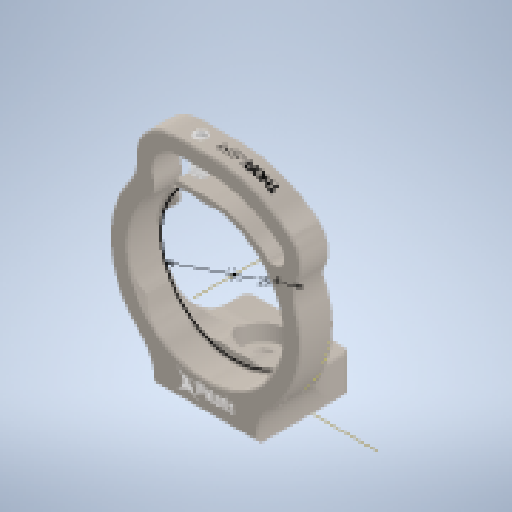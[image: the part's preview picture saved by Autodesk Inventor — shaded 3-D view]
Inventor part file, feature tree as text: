
AUTODESK INVENTOR PART (.ipt)
format: ipt  version: 2023 (Build 270158000, 158)  size: 2,079,232 bytes
history: native  units: mm
features: other x10, sketch x2
ambient origin geometry x8: Origin, YZ Plane, XZ Plane, XY Plane, X Axis, Y Axis, Z Axis, Center Point
bodies: Solid1 (feature_tree), Solid2 (feature_tree)
feature tree (12):
  sketch  "Sketch1"  dims[d3=25.4mm]
  other  "Work Point1"
  other  "Work Point2"
  other  "Work Point4"
  other  "Work Axis1"
  other  "Work Point7"
  sketch  "Sketch3"
  other  "Central Axis"
  other  "Work Point5"
  other  "Work Point6"
  other  "TTN111764-1-solid1"
  other  "SS4AR025-1-1-solid1"
